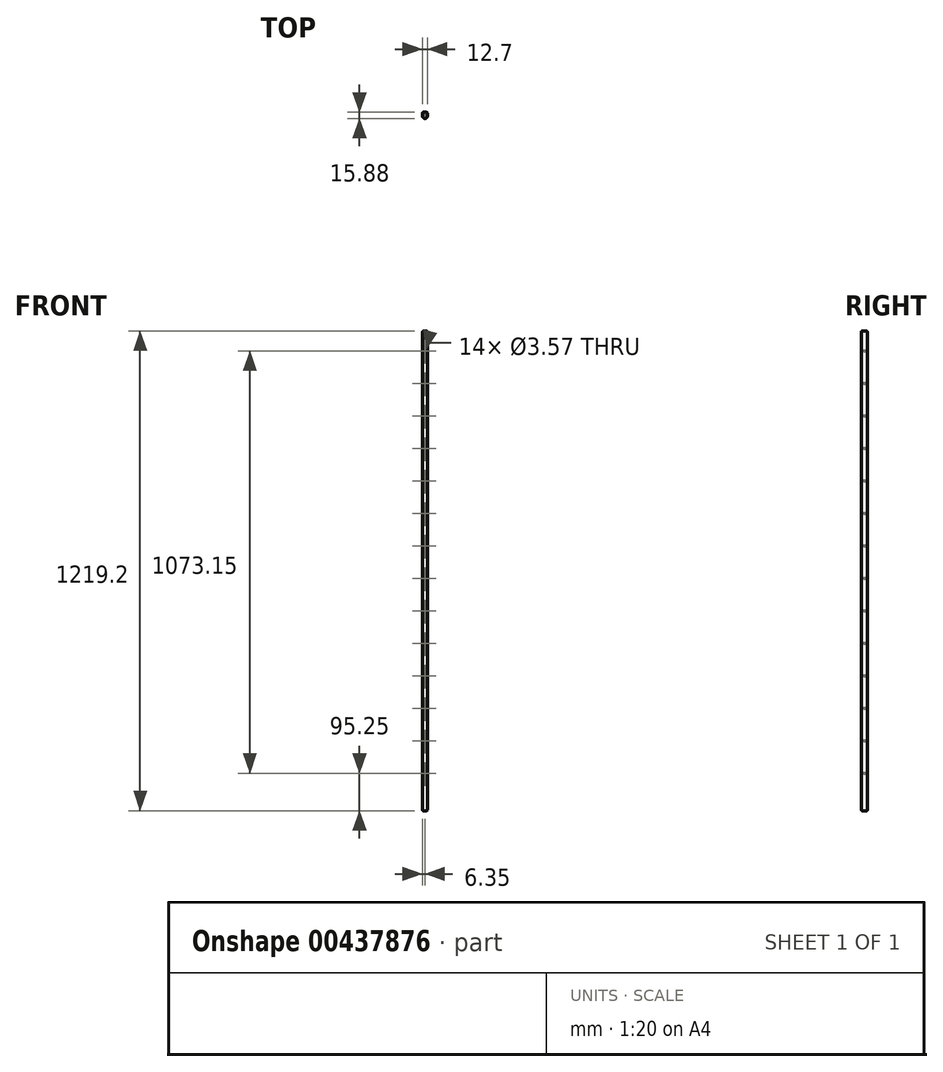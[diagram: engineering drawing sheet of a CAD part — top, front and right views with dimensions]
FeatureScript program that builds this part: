
annotation { "Feature Type Name" : "Feature", "Feature Type Description" : "" }
export const myFeature = defineFeature(function(context is Context, id is Id, definition is map)
    precondition{}
    {
        {
            var Q0;
            Q0=qCreatedBy(makeId("Top.planeOp"),FACE);
            var sketch = newSketch(context, id + "F0", { "sketchPlane" : qUnion([Q0])});
            skLineSegment(sketch, "E0.bottom", {"start": v(-6.35, 7.94) * mm, "end": v(6.35, 7.94) * mm});
            skLineSegment(sketch, "E0.top", {"start": v(-6.35, -7.94) * mm, "end": v(6.35, -7.94) * mm});
            skLineSegment(sketch, "E0.left", {"start": v(-6.35, 7.94) * mm, "end": v(-6.35, -7.94) * mm});
            skLineSegment(sketch, "E0.right", {"start": v(6.35, 7.94) * mm, "end": v(6.35, -7.94) * mm});
            skSolve(sketch);
        }
        {
            var Q0;
            Q0 = qSketchRegion(id + "F0", true);
            extrude(context, id + "F1", {"entities" : qUnion([Q0]), "depth" : 1219.2 * mm, "symmetric" : true});
        }
        {
            var Q0;
            Q0=makeQuery(id+"F1.opExtrude","SWEPT_EDGE",EDGE,{"disambiguationData":[OSD([sQuery(id+"F0.wireOp",EDGE,"E0.bottom"),sQuery(id+"F0.wireOp",EDGE,"E0.right")])]});
            var Q1;
            Q1=makeQuery(id+"F1.opExtrude","SWEPT_EDGE",EDGE,{"disambiguationData":[OSD([sQuery(id+"F0.wireOp",EDGE,"E0.bottom"),sQuery(id+"F0.wireOp",EDGE,"E0.left")])]});
            fillet(context, id + "F2", {"entities" : qUnion([Q0, Q1]), "radius" : 3.17 * mm, "tangentPropagation" : true, "allowEdgeOverflow" : false});
        }
        {
            var Q0;
            Q0=makeQuery(id+"F1.opExtrude","SWEPT_EDGE",EDGE,{"disambiguationData":[OSD([sQuery(id+"F0.wireOp",EDGE,"E0.top"),sQuery(id+"F0.wireOp",EDGE,"E0.left")])]});
            var Q1;
            Q1=makeQuery(id+"F1.opExtrude","SWEPT_EDGE",EDGE,{"disambiguationData":[OSD([sQuery(id+"F0.wireOp",EDGE,"E0.top"),sQuery(id+"F0.wireOp",EDGE,"E0.right")])]});
            fillet(context, id + "F3", {"entities" : qUnion([Q0, Q1]), "radius" : 6.35 * mm, "tangentPropagation" : true, "allowEdgeOverflow" : false});
        }
        {
            var Q0;
            Q0=makeQuery(id+"F1.opExtrude","CAP_FACE",FACE,{"disambiguationData":[OSD([sQuery(id+"F0.wireOp",EDGE,"E0.bottom"),sQuery(id+"F0.wireOp",EDGE,"E0.top"),sQuery(id+"F0.wireOp",EDGE,"E0.left"),sQuery(id+"F0.wireOp",EDGE,"E0.right")])],"isStart":false});
            var Q1;
            Q1=makeQuery(id+"F1.opExtrude","CAP_FACE",FACE,{"disambiguationData":[OSD([sQuery(id+"F0.wireOp",EDGE,"E0.bottom"),sQuery(id+"F0.wireOp",EDGE,"E0.top"),sQuery(id+"F0.wireOp",EDGE,"E0.left"),sQuery(id+"F0.wireOp",EDGE,"E0.right")])],"isStart":true});
            fillet(context, id + "F4", {"entities" : qUnion([Q0, Q1]), "radius" : 3.17 * mm, "tangentPropagation" : true, "allowEdgeOverflow" : false});
        }
        {
            var Q0;
            Q0=makeQuery(id+"F1.opExtrude","SWEPT_FACE",FACE,{"disambiguationData":[OSD([sQuery(id+"F0.wireOp",EDGE,"E0.bottom")])]});
            var sketch = newSketch(context, id + "F5", { "sketchPlane" : qUnion([Q0])});
            skPoint(sketch, "E1", {"position": v(0, 558.8) * mm});
            skPoint(sketch, "E2.1.0.0", {"position": v(0, 476.25) * mm});
            skPoint(sketch, "E2.2.0.0", {"position": v(0, 393.7) * mm});
            skLineSegment(sketch, "E2.direction1", {"start": v(0, 476.25) * mm, "end": v(0, 558.8) * mm, "construction": true});
            skPoint(sketch, "E3.0.3.0", {"position": v(0, 311.15) * mm});
            skPoint(sketch, "E3.0.4.0", {"position": v(0, 228.6) * mm});
            skPoint(sketch, "E3.0.5.0", {"position": v(0, 146.05) * mm});
            skPoint(sketch, "E3.0.6.0", {"position": v(0, 63.5) * mm});
            skPoint(sketch, "E3.0.7.0", {"position": v(0, -19.05) * mm});
            skPoint(sketch, "E3.0.8.0", {"position": v(0, -101.6) * mm});
            skPoint(sketch, "E3.0.9.0", {"position": v(0, -184.15) * mm});
            skPoint(sketch, "E3.0.10.0", {"position": v(0, -266.7) * mm});
            skPoint(sketch, "E3.0.11.0", {"position": v(0, -349.25) * mm});
            skPoint(sketch, "E4.0.12.0", {"position": v(0, -431.8) * mm});
            skPoint(sketch, "E4.0.13.0", {"position": v(0, -514.35) * mm});
            skSolve(sketch);
        }
        {
            var Q0;
            Q0=sQuery(id+"F5.wireOp",VERTEX,"E1");
            var Q1;
            Q1=sQuery(id+"F5.wireOp",VERTEX,"E2.1.0.0");
            var Q2;
            Q2=sQuery(id+"F5.wireOp",VERTEX,"E2.2.0.0");
            var Q3;
            Q3=sQuery(id+"F5.wireOp",VERTEX,"E3.0.3.0");
            var Q4;
            Q4=sQuery(id+"F5.wireOp",VERTEX,"E3.0.4.0");
            var Q5;
            Q5=sQuery(id+"F5.wireOp",VERTEX,"E3.0.5.0");
            var Q6;
            Q6=sQuery(id+"F5.wireOp",VERTEX,"E3.0.6.0");
            var Q7;
            Q7=sQuery(id+"F5.wireOp",VERTEX,"E3.0.7.0");
            var Q8;
            Q8=sQuery(id+"F5.wireOp",VERTEX,"E3.0.8.0");
            var Q9;
            Q9=sQuery(id+"F5.wireOp",VERTEX,"E3.0.9.0");
            var Q10;
            Q10=sQuery(id+"F5.wireOp",VERTEX,"E3.0.10.0");
            var Q11;
            Q11=sQuery(id+"F5.wireOp",VERTEX,"E3.0.11.0");
            var Q12;
            Q12=sQuery(id+"F5.wireOp",VERTEX,"E4.0.12.0");
            var Q13;
            Q13=sQuery(id+"F5.wireOp",VERTEX,"E4.0.13.0");
            var Q14;
            Q14=makeQuery(id+"F1.opExtrude","SWEPT_BODY",BODY,{"disambiguationData":[OSD([sQuery(id+"F0.wireOp",EDGE,"E0.bottom"),sQuery(id+"F0.wireOp",EDGE,"E0.top"),sQuery(id+"F0.wireOp",EDGE,"E0.left"),sQuery(id+"F0.wireOp",EDGE,"E0.right")])]});
            hole(context, id + "F6", {"style" : HoleStyle.SIMPLE, "endStyle" : HoleEndStyle.BLIND, "holeDiameter" : 3.57 * mm, "holeDepth" : 9.52 * mm, "isTappedThrough" : true, "tappedDepth" : 12.7 * mm, "tapClearance" : 3, "locations" : qUnion([Q0, Q1, Q2, Q3, Q4, Q5, Q6, Q7, Q8, Q9, Q10, Q11, Q12, Q13]), "scope" : qUnion([Q14])});
        }
    });
